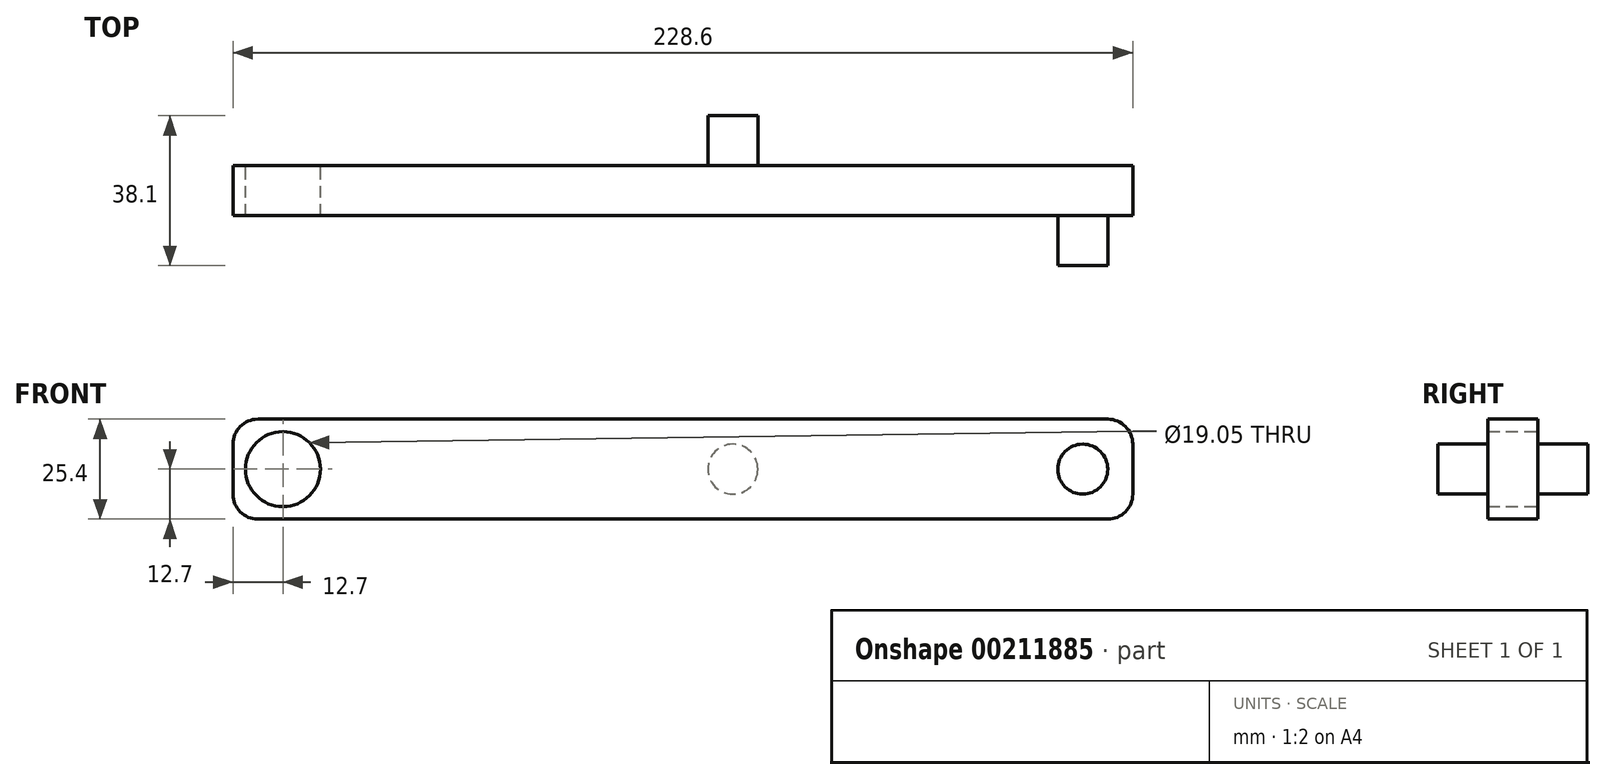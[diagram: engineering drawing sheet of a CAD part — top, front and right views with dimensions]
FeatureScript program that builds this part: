
annotation { "Feature Type Name" : "Feature", "Feature Type Description" : "" }
export const myFeature = defineFeature(function(context is Context, id is Id, definition is map)
    precondition{}
    {
        {
            var Q0;
            Q0=qCreatedBy(makeId("Front.planeOp"),FACE);
            var sketch = newSketch(context, id + "F0", { "sketchPlane" : qUnion([Q0])});
            skLineSegment(sketch, "E0.bottom", {"start": v(95.25, 12.7) * mm, "end": v(-120.65, 12.7) * mm});
            skLineSegment(sketch, "E0.top", {"start": v(95.25, -12.7) * mm, "end": v(-120.65, -12.7) * mm});
            skLineSegment(sketch, "E0.left", {"start": v(101.6, 6.35) * mm, "end": v(101.6, -6.35) * mm});
            skPoint(sketch, "E0.middle", {"position": v(0, 0) * mm});
            skCircle(sketch, "E1", {"center": v(-114.3, 0) * mm, "radius": 9.53 * mm});
            skPoint(sketch, "E2.visualSharp", {"position": v(-101.6, 12.7) * mm});
            skPoint(sketch, "E3.visualSharp", {"position": v(-101.6, -12.7) * mm});
            skPoint(sketch, "E4.visualSharp", {"position": v(101.6, 12.7) * mm});
            skArc(sketch, "E4.filletArc", {"start": v(101.6, 6.35) * mm, "mid": v(99.74, 10.84) * mm, "end": v(95.25, 12.7) * mm});
            skPoint(sketch, "E5.visualSharp", {"position": v(101.6, -12.7) * mm});
            skArc(sketch, "E5.filletArc", {"start": v(95.25, -12.7) * mm, "mid": v(99.74, -10.84) * mm, "end": v(101.6, -6.35) * mm});
            skLineSegment(sketch, "E6", {"start": v(-127, -6.35) * mm, "end": v(-127, 6.35) * mm});
            skPoint(sketch, "E7.visualSharp", {"position": v(-127, 12.7) * mm});
            skArc(sketch, "E7.filletArc", {"start": v(-120.65, 12.7) * mm, "mid": v(-125.14, 10.84) * mm, "end": v(-127, 6.35) * mm});
            skPoint(sketch, "E8.visualSharp", {"position": v(-127, -12.7) * mm});
            skArc(sketch, "E8.filletArc", {"start": v(-127, -6.35) * mm, "mid": v(-125.14, -10.84) * mm, "end": v(-120.65, -12.7) * mm});
            skSolve(sketch);
        }
        {
            var Q0;
            Q0=makeQuery(id+"F0.imprint","IMPRINT",FACE,{"disambiguationData":[TD([[makeQuery(id+"F0.imprint","IMPRINT",EDGE,{"derivedFrom":sQuery(id+"F0.wireOp",EDGE,"E0.bottom")}),1.0]])]});
            extrude(context, id + "F1", {"entities" : qUnion([Q0]), "endBound" : BoundingType.SYMMETRIC, "depth" : 12.7 * mm});
        }
        {
            var Q0;
            Q0=makeQuery(id+"F1.opExtrude","CAP_FACE",FACE,{"disambiguationData":[OSD([sQuery(id+"F0.wireOp",EDGE,"E0.bottom"),sQuery(id+"F0.wireOp",EDGE,"E0.top"),sQuery(id+"F0.wireOp",EDGE,"E0.left"),sQuery(id+"F0.wireOp",EDGE,"E0.right"),sQuery(id+"F0.wireOp",EDGE,"E1"),sQuery(id+"F0.wireOp",EDGE,"E2.filletArc"),sQuery(id+"F0.wireOp",EDGE,"E3.filletArc"),sQuery(id+"F0.wireOp",EDGE,"E4.filletArc"),sQuery(id+"F0.wireOp",EDGE,"E5.filletArc")])],"isStart":false});
            var sketch = newSketch(context, id + "F2", { "sketchPlane" : qUnion([Q0])});
            skCircle(sketch, "E9", {"center": v(88.9, 0) * mm, "radius": 6.35 * mm});
            skSolve(sketch);
        }
        {
            var Q0;
            Q0 = qSketchRegion(id + "F2", true);
            extrude(context, id + "F3", {"entities" : qUnion([Q0]), "operationType" : NewBodyOperationType.ADD, "depth" : 12.7 * mm});
        }
        {
            var Q0;
            Q0=makeQuery(id+"F1.opExtrude","CAP_FACE",FACE,{"disambiguationData":[OSD([sQuery(id+"F0.wireOp",EDGE,"E0.bottom"),sQuery(id+"F0.wireOp",EDGE,"E0.top"),sQuery(id+"F0.wireOp",EDGE,"E0.left"),sQuery(id+"F0.wireOp",EDGE,"E0.right"),sQuery(id+"F0.wireOp",EDGE,"E1"),sQuery(id+"F0.wireOp",EDGE,"E2.filletArc"),sQuery(id+"F0.wireOp",EDGE,"E3.filletArc"),sQuery(id+"F0.wireOp",EDGE,"E4.filletArc"),sQuery(id+"F0.wireOp",EDGE,"E5.filletArc")])],"isStart":true});
            var sketch = newSketch(context, id + "F4", { "sketchPlane" : qUnion([Q0])});
            skCircle(sketch, "E10", {"center": v(0, 0) * mm, "radius": 6.35 * mm});
            skSolve(sketch);
        }
        {
            var Q0;
            Q0 = qSketchRegion(id + "F4", true);
            extrude(context, id + "F5", {"entities" : qUnion([Q0]), "operationType" : NewBodyOperationType.ADD, "depth" : 12.7 * mm});
        }
    });
